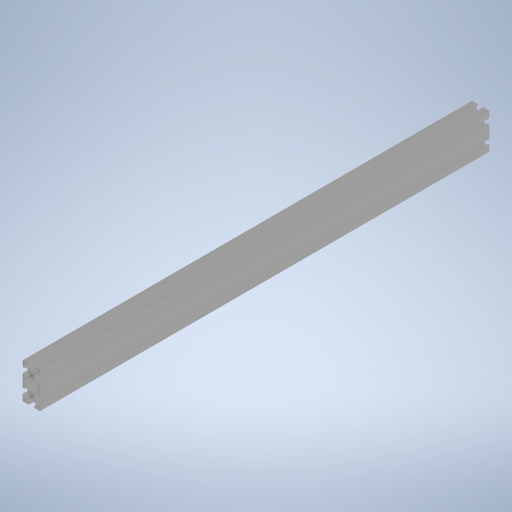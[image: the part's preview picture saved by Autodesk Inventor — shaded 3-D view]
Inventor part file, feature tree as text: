
AUTODESK INVENTOR PART (.ipt)
format: ipt  version: 2024 (Build 280153000, 153)  size: 473,600 bytes
history: native  units: mm
features: other x7, sketch x2, extrude x1, hole x1, pattern_linear x1, mirror x1
ambient origin geometry x8: Origin, YZ Plane, XZ Plane, XY Plane, X Axis, Y Axis, Z Axis, Center Point
bodies: Solid1 (feature_tree)
feature tree (13):
  extrude  "Extrusion1"  Depth=20.0mm TaperAngle=0.0deg
  hole  "Hole1"  [1 undecoded]
  pattern_linear  "Rectangular Pattern1"  [2 undecoded]
  other  "C1_XY"
  other  "C1_YZ"
  other  "C1_ZX"
  other  "C1_X"
  other  "C1_Y"
  other  "C1_Z"
  other  "C1_Center"
  mirror  "Mirror1"
  sketch  "Sketch_1"  dims[d0=500.0mm d1=0.0mm]
  sketch  "Sketch2"  dims[d2=4.134mm d3=10.0mm d4=4.0mm d5=2.0mm d6=90.0deg d7=500.0mm d8=0.0mm d9=20.0mm d11=20.0mm d12=10.0mm d14=0.0mm d15=0.0mm]
note: 3 required parameter values undecoded (feature->parameter linkage not recoverable at this tier; creation-order binding heuristic only, values carry confidence <= 0.55)
